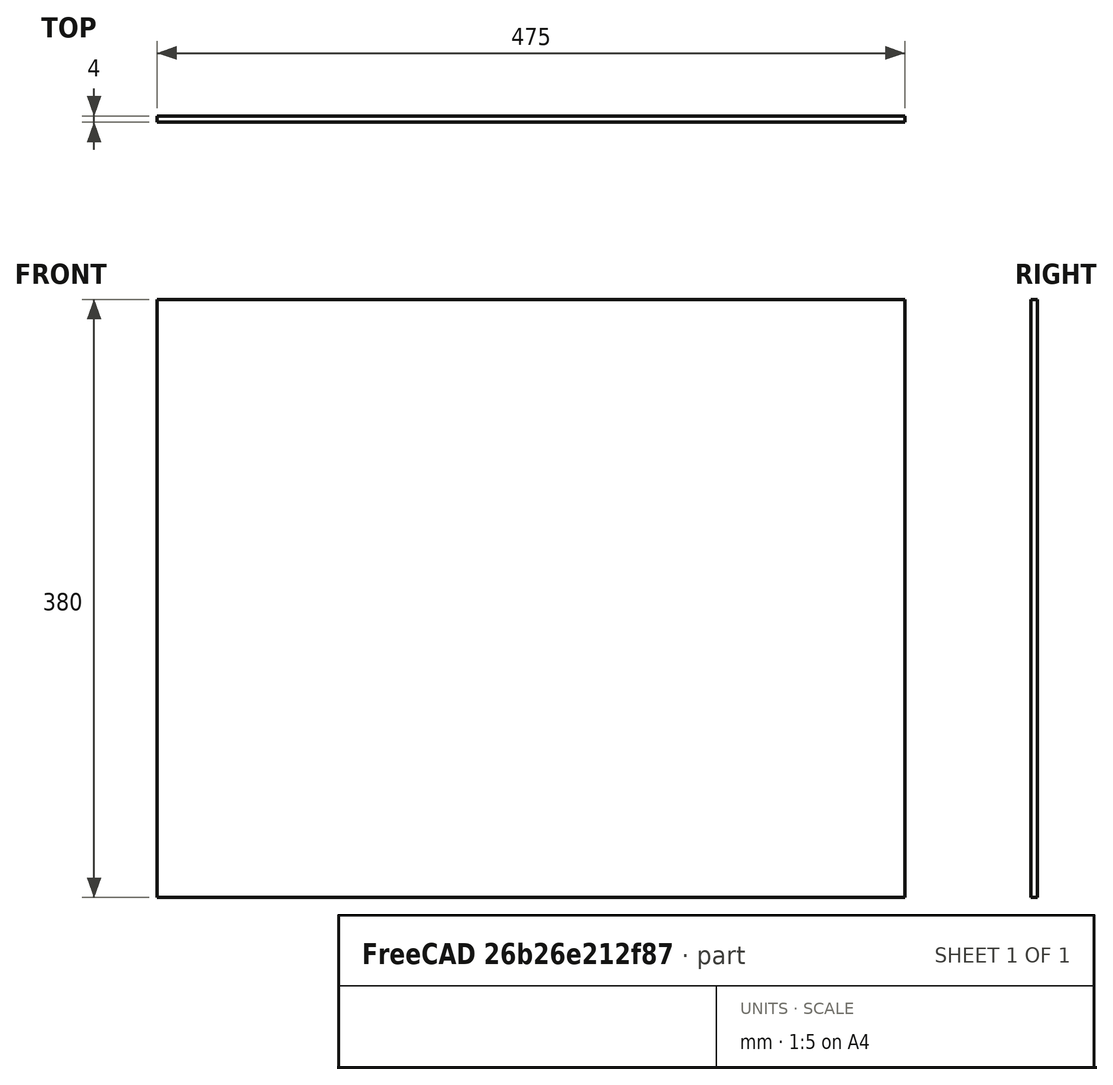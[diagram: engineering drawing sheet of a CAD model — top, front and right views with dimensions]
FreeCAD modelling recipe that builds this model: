
FCSTD DOCUMENT  (FreeCAD 0.18R4 (GitTag))
Label: door_glass
License: All rights reserved
LicenseURL: http://en.wikipedia.org/wiki/All_rights_reserved
objects: Sketcher::SketchObject×1, PartDesign::Pad×1, PartDesign::Body×1
note: 4 computed .brp shape members not serialized (recipe doc carries the construction recipe); baked Part::Feature solids carry a one-line shape summary decoded from their .brp

FEATURE [Sketcher::SketchObject] Sketch
  MapMode = 5
  Placement = pos=(0,0,0) rot=(1,0,0;1.5708rad)
  Support = -> [XZ_Plane]
  sketch-geometry (4):
    g0: LineSegment StartX=0 StartY=0 StartZ=0 EndX=-475 EndY=0 EndZ=0
    g1: LineSegment StartX=-475 StartY=0 StartZ=0 EndX=-475 EndY=380 EndZ=0
    g2: LineSegment StartX=-475 StartY=380 StartZ=0 EndX=0 EndY=380 EndZ=0
    g3: LineSegment StartX=0 StartY=380 StartZ=0 EndX=0 EndY=0 EndZ=0
  constraints (11):
    c: Coincident(g0,g1)
    c: Coincident(g1,g2)
    c: Coincident(g2,g3)
    c: Coincident(g3,g0)
    c: Horizontal(g0)
    c: Horizontal(g2)
    c: Vertical(g1)
    c: Vertical(g3)
    c: Coincident(g0,g-1)
    c: DistanceX(g0,g0) = 475
    c: DistanceY(g3,g3) = 380
FEATURE [PartDesign::Pad] Pad
  Length = 4
  Length2 = 100
  Placement = pos=(0,0,0) rot=(1,0,0;1.5708rad)
  Profile = -> Sketch
  Type = 0
FEATURE [PartDesign::Body] Body
  Group = -> [Sketch,Pad]
  Origin = -> Origin
  Tip = -> Pad
